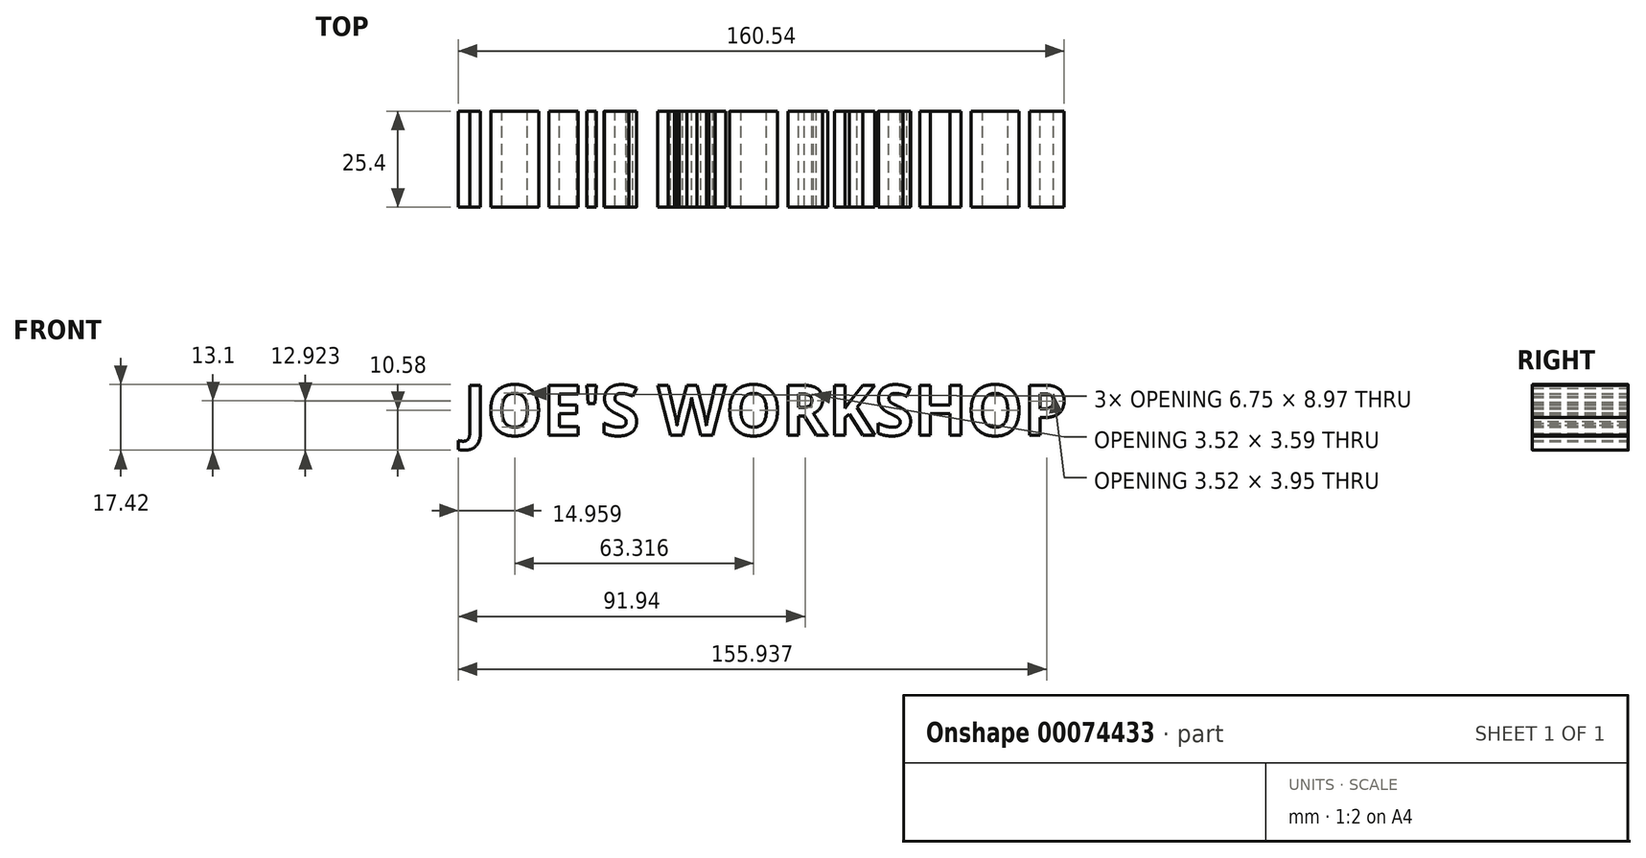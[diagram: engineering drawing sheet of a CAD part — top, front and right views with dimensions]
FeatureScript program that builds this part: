
annotation { "Feature Type Name" : "Feature", "Feature Type Description" : "" }
export const myFeature = defineFeature(function(context is Context, id is Id, definition is map)
    precondition{}
    {
        {
            var Q0;
            Q0=qCreatedBy(makeId("Front.planeOp"),FACE);
            var sketch = newSketch(context, id + "F0", { "sketchPlane" : qUnion([Q0])});
            skText(sketch, "E0", { "text": "JOE\'S WORKSHOP", "fontName": "OpenSans-Bold.ttf"});
            const initialGuessF0  = {"E0": [-0.09816, 0.04224, 1, 0, 0.01341]};
            skSetInitialGuess(sketch, initialGuessF0);
            skSolve(sketch);
        }
        {
            var Q0;
            Q0 = qSketchRegion(id + "F0", true);
            extrude(context, id + "F1", {"entities" : qUnion([Q0]), "depth" : 25.4 * mm});
        }
    });
